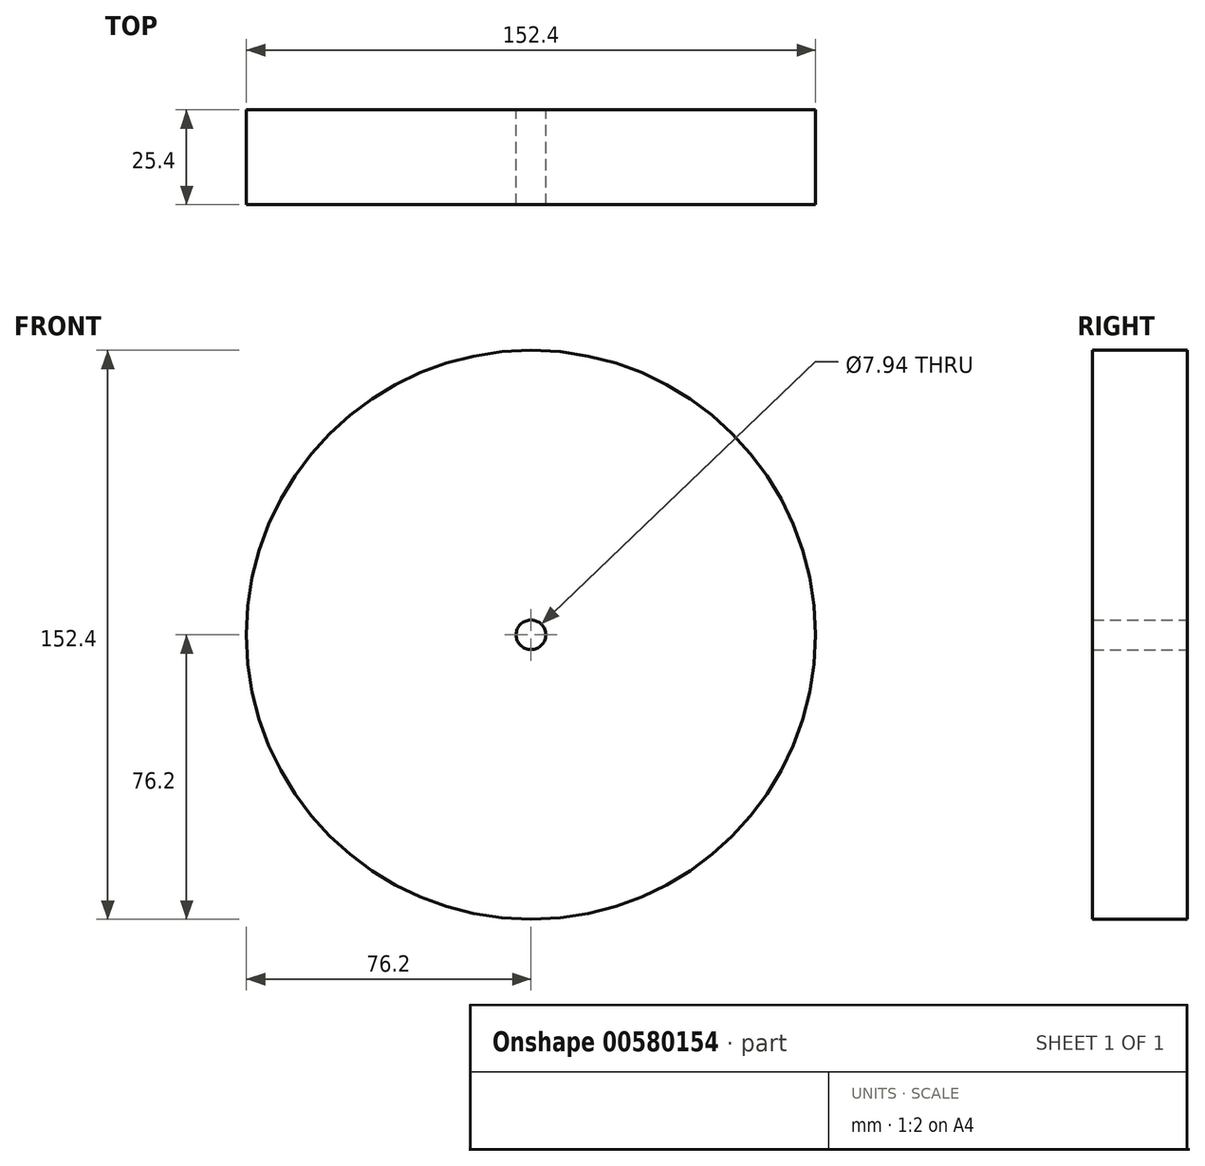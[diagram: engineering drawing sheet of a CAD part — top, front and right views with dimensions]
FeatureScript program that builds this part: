
annotation { "Feature Type Name" : "Feature", "Feature Type Description" : "" }
export const myFeature = defineFeature(function(context is Context, id is Id, definition is map)
    precondition{}
    {
        {
            var Q0;
            Q0=qCreatedBy(makeId("Front.planeOp"),FACE);
            var sketch = newSketch(context, id + "F0", { "sketchPlane" : qUnion([Q0])});
            skCircle(sketch, "E0", {"center": v(0, 0) * mm, "radius": 76.2 * mm});
            skCircle(sketch, "E1", {"center": v(0, 0) * mm, "radius": 3.97 * mm});
            skSolve(sketch);
        }
        {
            var Q0;
            Q0=qSketchRegion(id+"F0",true);
            extrude(context, id + "F1", {"entities" : qUnion([Q0]), "depth" : 25.4 * mm, "symmetric" : true});
        }
    });
